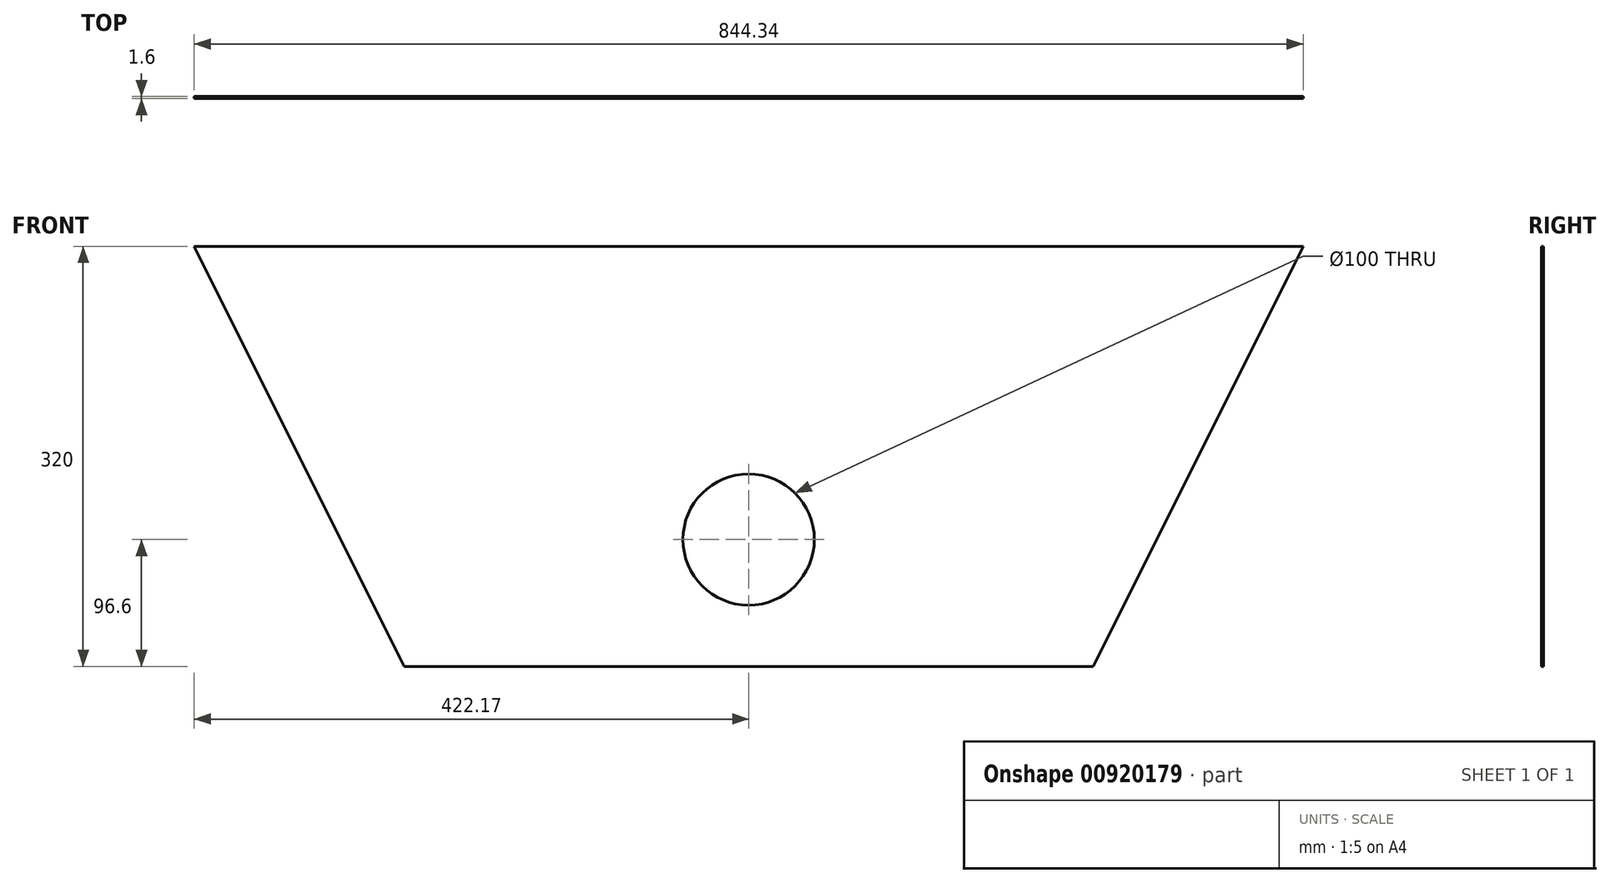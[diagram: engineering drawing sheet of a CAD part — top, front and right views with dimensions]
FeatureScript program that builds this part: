
annotation { "Feature Type Name" : "Feature", "Feature Type Description" : "" }
export const myFeature = defineFeature(function(context is Context, id is Id, definition is map)
    precondition{}
    {
        {
            var Q0;
            Q0=qCreatedBy(makeId("Front.planeOp"),FACE);
            var sketch = newSketch(context, id + "F0", { "sketchPlane" : qUnion([Q0])});
            skLineSegment(sketch, "E0", {"start": v(-422.17, 181.87) * mm, "end": v(-262.17, -138.13) * mm});
            skLineSegment(sketch, "E1", {"start": v(422.17, 181.87) * mm, "end": v(262.17, -138.13) * mm});
            skLineSegment(sketch, "E2", {"start": v(262.17, -138.13) * mm, "end": v(-262.17, -138.13) * mm});
            skLineSegment(sketch, "E3", {"start": v(422.17, 181.87) * mm, "end": v(-422.17, 181.87) * mm});
            skCircle(sketch, "E4", {"center": v(0, -41.53) * mm, "radius": 50 * mm});
            skPoint(sketch, "E5.orphan", {"position": v(0, -138.13) * mm});
            skSolve(sketch);
        }
        {
            var Q0;
            Q0=qSketchRegion(id+"F0",true);
            extrude(context, id + "F1", {"entities" : qUnion([Q0]), "depth" : 1.6 * mm, "offsetDistance" : 25 * mm});
        }
    });
